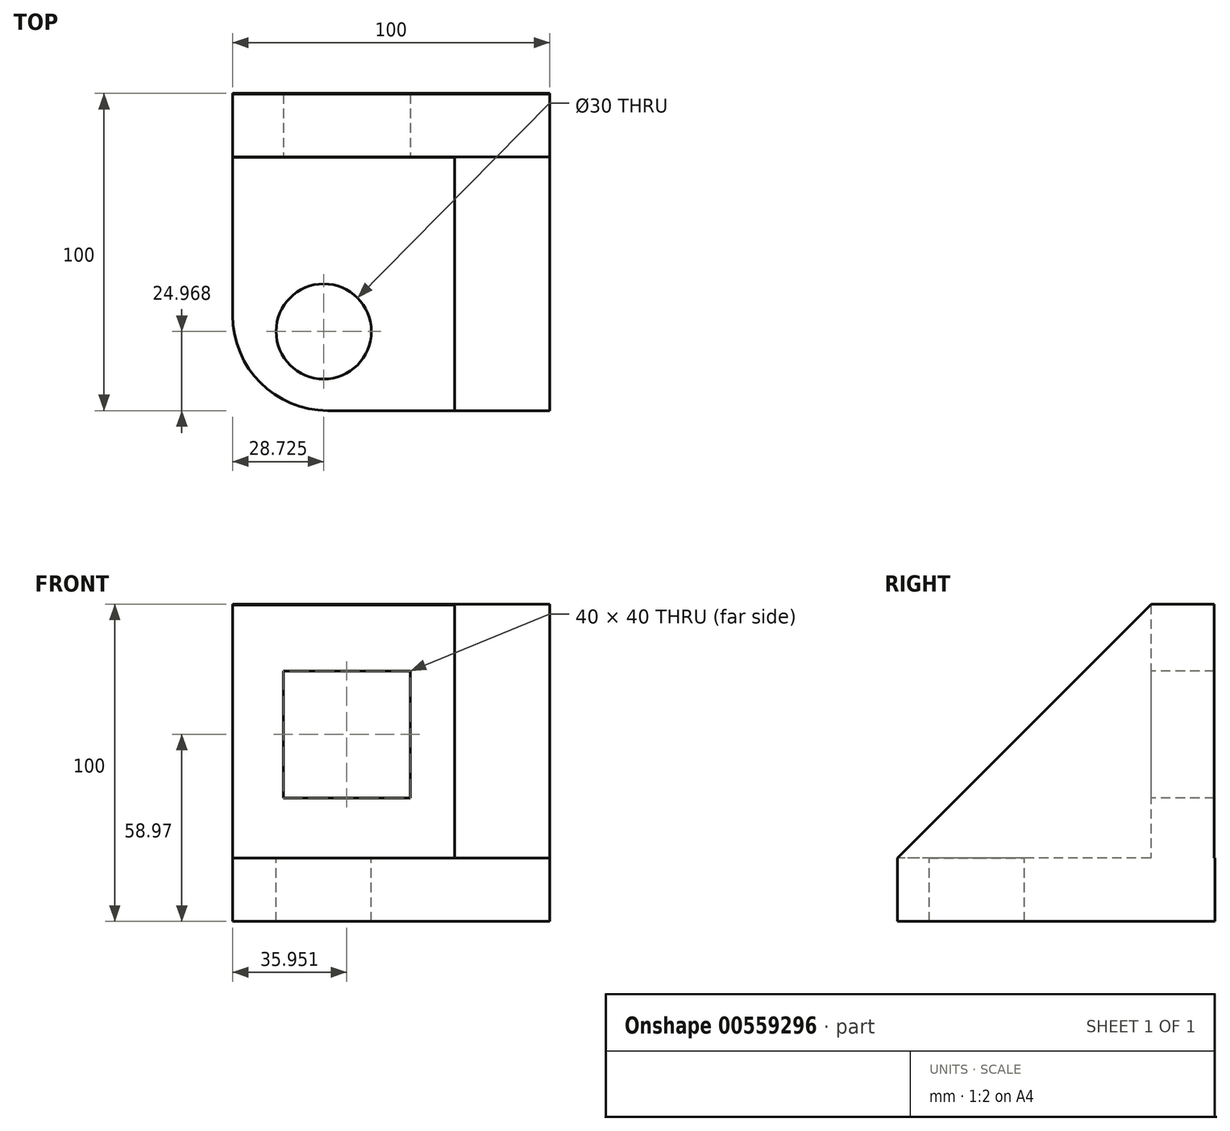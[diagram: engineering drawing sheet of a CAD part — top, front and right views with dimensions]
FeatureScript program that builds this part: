
annotation { "Feature Type Name" : "Feature", "Feature Type Description" : "" }
export const myFeature = defineFeature(function(context is Context, id is Id, definition is map)
    precondition{}
    {
        {
            var Q0;
            Q0=qCreatedBy(makeId("Top.planeOp"),FACE);
            var sketch = newSketch(context, id + "F0", { "sketchPlane" : qUnion([Q0])});
            skLineSegment(sketch, "E0.bottom", {"start": v(-50, 50) * mm, "end": v(50, 50) * mm});
            skLineSegment(sketch, "E0.top", {"start": v(-50, -50) * mm, "end": v(50, -50) * mm});
            skLineSegment(sketch, "E0.left", {"start": v(-50, 50) * mm, "end": v(-50, -50) * mm});
            skLineSegment(sketch, "E0.right", {"start": v(50, 50) * mm, "end": v(50, -50) * mm});
            skPoint(sketch, "E0.middle", {"position": v(0, 0) * mm});
            skSolve(sketch);
        }
        {
            var Q0;
            Q0=makeQuery(id+"F0.imprint","IMPRINT",FACE,{"disambiguationData":[TD([[makeQuery(id+"F0.imprint","IMPRINT",EDGE,{"derivedFrom":sQuery(id+"F0.wireOp",EDGE,"E0.bottom")}),-1.0]])]});
            extrude(context, id + "F1", {"entities" : qUnion([Q0]), "depth" : 20 * mm, "offsetDistance" : 25 * mm});
        }
        {
            var Q0;
            Q0=makeQuery(id+"F1.opExtrude","SWEPT_EDGE",EDGE,{"disambiguationData":[OSD([sQuery(id+"F0.wireOp",EDGE,"E0.top"),sQuery(id+"F0.wireOp",EDGE,"E0.left")])]});
            fillet(context, id + "F2", {"entities" : qUnion([Q0]), "radius" : 30 * mm, "tangentPropagation" : true, "allowEdgeOverflow" : false});
        }
        {
            var Q0;
            Q0=qCreatedBy(makeId("Top.planeOp"),FACE);
            var sketch = newSketch(context, id + "F3", { "sketchPlane" : qUnion([Q0])});
            skLineSegment(sketch, "E1.bottom", {"start": v(-50, 49.8) * mm, "end": v(50, 49.8) * mm});
            skLineSegment(sketch, "E1.top", {"start": v(-50, 29.8) * mm, "end": v(50, 29.8) * mm});
            skLineSegment(sketch, "E1.left", {"start": v(-50, 49.8) * mm, "end": v(-50, 29.8) * mm});
            skLineSegment(sketch, "E1.right", {"start": v(50, 49.8) * mm, "end": v(50, 29.8) * mm});
            skSolve(sketch);
        }
        {
            var Q0;
            Q0=makeQuery(id+"F3.imprint","IMPRINT",FACE,{"disambiguationData":[TD([[makeQuery(id+"F3.imprint","IMPRINT",EDGE,{"derivedFrom":sQuery(id+"F3.wireOp",EDGE,"E1.bottom")}),-1.0]])]});
            extrude(context, id + "F4", {"entities" : qUnion([Q0]), "operationType" : NewBodyOperationType.ADD, "depth" : 100 * mm, "offsetDistance" : 25 * mm});
        }
        {
            var Q0;
            {var subQ0=sQuery(id+"F0.wireOp",EDGE,"E0.left");var subQ1=sQuery(id+"F0.wireOp",EDGE,"E0.top");var subQ2=sQuery(id+"F0.wireOp",EDGE,"E0.right");Q0=makeQuery(id+"F4.boolean.opBoolean","SPLIT",FACE,{"disambiguationData":[TD([makeQuery(id+"F1.opExtrude","SWEPT_FACE",FACE,{"disambiguationData":[OSD([subQ1])]})])],"derivedFrom":makeQuery(id+"F1.opExtrude","CAP_FACE",FACE,{"disambiguationData":[OSD([sQuery(id+"F0.wireOp",EDGE,"E0.bottom"),subQ1,subQ0,subQ2])],"isStart":false})});}
            var sketch = newSketch(context, id + "F5", { "sketchPlane" : qUnion([Q0])});
            skLineSegment(sketch, "E2.bottom", {"start": v(20, 29.8) * mm, "end": v(50, 29.8) * mm});
            skLineSegment(sketch, "E2.top", {"start": v(20, -50.2) * mm, "end": v(50, -50.2) * mm});
            skLineSegment(sketch, "E2.left", {"start": v(20, 29.8) * mm, "end": v(20, -50.2) * mm});
            skLineSegment(sketch, "E2.right", {"start": v(50, 29.8) * mm, "end": v(50, -50.2) * mm});
            skSolve(sketch);
        }
        {
            var Q0;
            {var subQ0=sQuery(id+"F5.wireOp",EDGE,"E2.bottom");Q0=makeQuery(id+"F5.imprint","IMPRINT",FACE,{"disambiguationData":[TD([[makeQuery(id+"F5.imprint","IMPRINT",EDGE,{"derivedFrom":subQ0}),1.0]])]});}
            extrude(context, id + "F6", {"entities" : qUnion([Q0]), "operationType" : NewBodyOperationType.ADD, "depth" : 80 * mm, "offsetDistance" : 25 * mm});
        }
        {
            var Q0;
            Q0=makeQuery(id+"F6.opExtrude","CAP_EDGE",EDGE,{"disambiguationData":[OSD([sQuery(id+"F0.wireOp",EDGE,"E0.top")])],"isStart":false});
            chamfer(context, id + "F7", {"entities" : qUnion([Q0]), "width" : 80 * mm, "tangentPropagation" : true});
        }
        {
            var Q0;
            {var subQ0=sQuery(id+"F0.wireOp",EDGE,"E0.left");var subQ1=sQuery(id+"F0.wireOp",EDGE,"E0.top");var subQ2=sQuery(id+"F0.wireOp",EDGE,"E0.right");Q0=makeQuery(id+"F4.boolean.opBoolean","SPLIT",FACE,{"disambiguationData":[TD([makeQuery(id+"F1.opExtrude","SWEPT_FACE",FACE,{"disambiguationData":[OSD([subQ1])]})])],"derivedFrom":makeQuery(id+"F1.opExtrude","CAP_FACE",FACE,{"disambiguationData":[OSD([sQuery(id+"F0.wireOp",EDGE,"E0.bottom"),subQ1,subQ0,subQ2])],"isStart":false})});}
            var sketch = newSketch(context, id + "F8", { "sketchPlane" : qUnion([Q0])});
            skCircle(sketch, "E3", {"center": v(-21.28, -25.03) * mm, "radius": 15 * mm});
            skSolve(sketch);
        }
        {
            var Q0;
            Q0=makeQuery(id+"F8.imprint","IMPRINT",FACE,{"disambiguationData":[TD([[makeQuery(id+"F8.imprint","IMPRINT",EDGE,{"derivedFrom":sQuery(id+"F8.wireOp",EDGE,"E3")}),1.0]])]});
            extrude(context, id + "F9", {"entities" : qUnion([Q0]), "operationType" : NewBodyOperationType.REMOVE, "oppositeDirection" : true, "depth" : 61.3 * mm, "offsetDistance" : 25 * mm});
        }
        {
            var Q0;
            Q0=makeQuery(id+"F4.opExtrude","SWEPT_FACE",FACE,{"disambiguationData":[OSD([sQuery(id+"F3.wireOp",EDGE,"E1.top")])]});
            var sketch = newSketch(context, id + "F10", { "sketchPlane" : qUnion([Q0])});
            skLineSegment(sketch, "E4.bottom", {"start": v(-34.05, 78.97) * mm, "end": v(5.95, 78.97) * mm});
            skLineSegment(sketch, "E4.top", {"start": v(-34.05, 38.97) * mm, "end": v(5.95, 38.97) * mm});
            skLineSegment(sketch, "E4.left", {"start": v(-34.05, 78.97) * mm, "end": v(-34.05, 38.97) * mm});
            skLineSegment(sketch, "E4.right", {"start": v(5.95, 78.97) * mm, "end": v(5.95, 38.97) * mm});
            skSolve(sketch);
        }
        {
            var Q0;
            Q0=makeQuery(id+"F10.imprint","IMPRINT",FACE,{"disambiguationData":[TD([[makeQuery(id+"F10.imprint","IMPRINT",EDGE,{"derivedFrom":sQuery(id+"F10.wireOp",EDGE,"E4.bottom")}),-1.0]])]});
            extrude(context, id + "F11", {"entities" : qUnion([Q0]), "operationType" : NewBodyOperationType.REMOVE, "oppositeDirection" : true, "depth" : 41.8 * mm, "offsetDistance" : 25 * mm});
        }
    });
